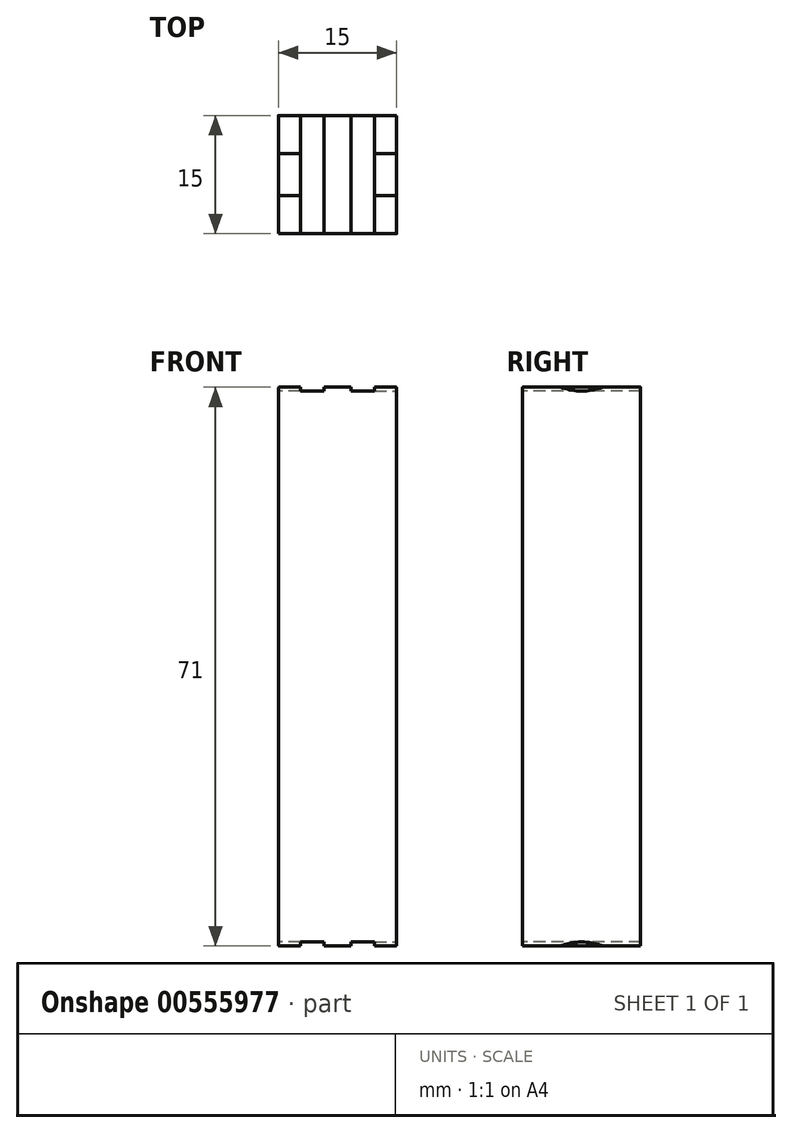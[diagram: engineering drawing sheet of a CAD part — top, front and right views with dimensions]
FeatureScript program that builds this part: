
annotation { "Feature Type Name" : "Feature", "Feature Type Description" : "" }
export const myFeature = defineFeature(function(context is Context, id is Id, definition is map)
    precondition{}
    {
        {
            assignVariable(context, id + "F0", {"name" : "length", "anyValue" : 30});
        }
        {
            var Q0;
            Q0=qCreatedBy(makeId("Right.planeOp"),FACE);
            var sketch = newSketch(context, id + "F1", { "sketchPlane" : qUnion([Q0])});
            skArc(sketch, "E0", {"start": v(7.5, 0) * mm, "mid": v(0, 7.5) * mm, "end": v(-7.5, 0) * mm});
            skCircle(sketch, "E1", {"center": v(0, 0) * mm, "radius": 2.5 * mm});
            skLineSegment(sketch, "E2", {"start": v(-7.5, 0) * mm, "end": v(-7.5, -12.5) * mm});
            skLineSegment(sketch, "E3", {"start": v(7.5, 0) * mm, "end": v(7.5, -12.5) * mm});
            skLineSegment(sketch, "E4", {"start": v(7.5, -12.5) * mm, "end": v(-7.5, -12.5) * mm});
            skSolve(sketch);
        }
        {
            var Q0;
            Q0=makeQuery(id+"F1.imprint","IMPRINT",FACE,{"disambiguationData":[TD([[makeQuery(id+"F1.imprint","IMPRINT",EDGE,{"derivedFrom":sQuery(id+"F1.wireOp",EDGE,"E0")}),1.0]])]});
            extrude(context, id + "F2", {"entities" : qUnion([Q0]), "depth" : 15 * mm, "symmetric" : true});
        }
        {
            var Q0;
            Q0=qCreatedBy(makeId("Front.planeOp"),FACE);
            var sketch = newSketch(context, id + "F3", { "sketchPlane" : qUnion([Q0])});
            skLineSegment(sketch, "E5", {"start": v(0, -18.95) * mm, "end": v(0, 19.26) * mm, "construction": true});
            skLineSegment(sketch, "E6", {"start": v(-12.45, 0) * mm, "end": v(16.05, 0) * mm, "construction": true});
            skLineSegment(sketch, "E7.0", {"start": v(-1.7, -7) * mm, "end": v(-1.7, 8.45) * mm});
            skLineSegment(sketch, "E8.0.MirrorCS", {"start": v(1.7, -7) * mm, "end": v(1.7, 8.45) * mm});
            skLineSegment(sketch, "E9.0", {"start": v(-8.58, -7) * mm, "end": v(-4.7, -7) * mm});
            skLineSegment(sketch, "E10.0", {"start": v(4.7, -7) * mm, "end": v(4.7, 8.45) * mm});
            skLineSegment(sketch, "E11.0", {"start": v(-4.7, -7) * mm, "end": v(-4.7, 8.45) * mm});
            skPoint(sketch, "E12.orphan", {"position": v(-1.7, -18.95) * mm});
            skLineSegment(sketch, "E13.trimOffspring", {"start": v(4.7, -7) * mm, "end": v(8.53, -7) * mm});
            skPoint(sketch, "E14.orphan", {"position": v(1.7, -18.95) * mm});
            skLineSegment(sketch, "E15", {"start": v(-8.58, 8.45) * mm, "end": v(-4.7, 8.45) * mm});
            skLineSegment(sketch, "E16", {"start": v(8.53, 8.45) * mm, "end": v(8.53, -7) * mm});
            skLineSegment(sketch, "E17", {"start": v(-8.58, -7) * mm, "end": v(-8.58, 8.45) * mm});
            skLineSegment(sketch, "E18.trimOffspring", {"start": v(-1.7, 8.45) * mm, "end": v(1.7, 8.45) * mm});
            skPoint(sketch, "E19.orphan", {"position": v(-1.7, 19.26) * mm});
            skPoint(sketch, "E20.orphan", {"position": v(1.7, 19.26) * mm});
            skLineSegment(sketch, "E21.trimOffspring", {"start": v(4.7, 8.45) * mm, "end": v(8.53, 8.45) * mm});
            skLineSegment(sketch, "E22", {"start": v(1.7, -7) * mm, "end": v(-1.7, -7) * mm});
            skSolve(sketch);
        }
        {
            var Q0;
            {Q0=qUnion([makeQuery(id+"F3.imprint","IMPRINT",FACE,{"disambiguationData":[TD([[makeQuery(id+"F3.imprint","IMPRINT",EDGE,{"derivedFrom":sQuery(id+"F3.wireOp",EDGE,"E7.0")}),-1.0]])]}),makeQuery(id+"F3.imprint","IMPRINT",FACE,{"disambiguationData":[TD([[makeQuery(id+"F3.imprint","IMPRINT",EDGE,{"derivedFrom":sQuery(id+"F3.wireOp",EDGE,"E9.0")}),1.0]])]}),makeQuery(id+"F3.imprint","IMPRINT",FACE,{"disambiguationData":[TD([[makeQuery(id+"F3.imprint","IMPRINT",EDGE,{"derivedFrom":sQuery(id+"F3.wireOp",EDGE,"E10.0")}),-1.0]])]})]);}
            extrude(context, id + "F4", {"entities" : qUnion([Q0]), "operationType" : NewBodyOperationType.REMOVE, "oppositeDirection" : true, "depth" : 32.83 * mm, "symmetric" : true});
        }
        {
            var Q0;
            Q0=makeQuery(id+"F2.opExtrude","CAP_FACE",FACE,{"disambiguationData":[OSD([sQuery(id+"F1.wireOp",EDGE,"E0"),sQuery(id+"F1.wireOp",EDGE,"E1"),sQuery(id+"F1.wireOp",EDGE,"E2"),sQuery(id+"F1.wireOp",EDGE,"E3"),sQuery(id+"F1.wireOp",EDGE,"E4")])],"isStart":true});
            var sketch = newSketch(context, id + "F5", { "sketchPlane" : qUnion([Q0])});
            skCircle(sketch, "E23", {"center": v(0, 0) * mm, "radius": 7.5 * mm});
            skSolve(sketch);
        }
        {
            var Q0;
            {var subQ0=makeQuery(id+"F4.boolean.opBoolean","INTERSECT",EDGE,{"derivedFrom":[makeQuery(id+"F2.opExtrude","CAP_FACE",FACE,{"disambiguationData":[OSD([sQuery(id+"F1.wireOp",EDGE,"E0"),sQuery(id+"F1.wireOp",EDGE,"E1"),sQuery(id+"F1.wireOp",EDGE,"E2"),sQuery(id+"F1.wireOp",EDGE,"E3"),sQuery(id+"F1.wireOp",EDGE,"E4")])],"isStart":true}),makeQuery(id+"F4.opExtrude","SWEPT_FACE",FACE,{"disambiguationData":[OSD([sQuery(id+"F3.wireOp",EDGE,"E9.0")])]})]});var subQ1=sQuery(id+"F5.wireOp",EDGE,"E23");var subQ3=makeQuery(id+"F5.imprint","INTERSECT",VERTEX,{"disambiguationData":[OD(0.0)],"derivedFrom":[subQ0,subQ1]});Q0=qUnion([makeQuery(id+"F5.imprint","IMPRINT",FACE,{"disambiguationData":[TD([[makeQuery(id+"F5.imprint","IMPRINT",EDGE,{"disambiguationData":[TD([[subQ3,-1.0]])],"derivedFrom":subQ1}),1.0]])]}),makeQuery(id+"F5.imprint","IMPRINT",FACE,{"disambiguationData":[TD([[makeQuery(id+"F5.imprint","IMPRINT",EDGE,{"disambiguationData":[TD([[subQ3,1.0]])],"derivedFrom":subQ1}),1.0]])]})]);}
            var Q1;
            Q1=makeQuery(id+"F4.boolean.opBoolean","COPY",FACE,{"derivedFrom":makeQuery(id+"F4.opExtrude","SWEPT_FACE",FACE,{"disambiguationData":[OSD([sQuery(id+"F3.wireOp",EDGE,"E11.0")])]})});
            extrude(context, id + "F6", {"entities" : qUnion([Q0]), "operationType" : NewBodyOperationType.REMOVE, "endBound" : BoundingType.UP_TO_SURFACE, "oppositeDirection" : true, "endBoundEntityFace" : qUnion([Q1]), "depth" : 25 * mm});
        }
        {
            var Q0;
            Q0=makeQuery(id+"F2.opExtrude","CAP_FACE",FACE,{"disambiguationData":[OSD([sQuery(id+"F1.wireOp",EDGE,"E0"),sQuery(id+"F1.wireOp",EDGE,"E1"),sQuery(id+"F1.wireOp",EDGE,"E2"),sQuery(id+"F1.wireOp",EDGE,"E3"),sQuery(id+"F1.wireOp",EDGE,"E4")])],"isStart":false});
            var sketch = newSketch(context, id + "F7", { "sketchPlane" : qUnion([Q0])});
            skCircle(sketch, "E24", {"center": v(0, 0) * mm, "radius": 7.5 * mm});
            skSolve(sketch);
        }
        {
            var Q0;
            {var subQ0=makeQuery(id+"F4.boolean.opBoolean","INTERSECT",EDGE,{"derivedFrom":[makeQuery(id+"F2.opExtrude","CAP_FACE",FACE,{"disambiguationData":[OSD([sQuery(id+"F1.wireOp",EDGE,"E0"),sQuery(id+"F1.wireOp",EDGE,"E1"),sQuery(id+"F1.wireOp",EDGE,"E2"),sQuery(id+"F1.wireOp",EDGE,"E3"),sQuery(id+"F1.wireOp",EDGE,"E4")])],"isStart":false}),makeQuery(id+"F4.opExtrude","SWEPT_FACE",FACE,{"disambiguationData":[OSD([sQuery(id+"F3.wireOp",EDGE,"E13.trimOffspring")])]})]});var subQ1=sQuery(id+"F7.wireOp",EDGE,"E24");var subQ3=makeQuery(id+"F7.imprint","INTERSECT",VERTEX,{"disambiguationData":[OD(0.0)],"derivedFrom":[subQ0,subQ1]});Q0=qUnion([makeQuery(id+"F7.imprint","IMPRINT",FACE,{"disambiguationData":[TD([[makeQuery(id+"F7.imprint","IMPRINT",EDGE,{"disambiguationData":[TD([[subQ3,1.0]])],"derivedFrom":subQ1}),1.0]])]}),makeQuery(id+"F7.imprint","IMPRINT",FACE,{"disambiguationData":[TD([[makeQuery(id+"F7.imprint","IMPRINT",EDGE,{"disambiguationData":[TD([[subQ3,-1.0]])],"derivedFrom":subQ1}),1.0]])]})]);}
            var Q1;
            Q1=makeQuery(id+"F4.boolean.opBoolean","COPY",FACE,{"derivedFrom":makeQuery(id+"F4.opExtrude","SWEPT_FACE",FACE,{"disambiguationData":[OSD([sQuery(id+"F3.wireOp",EDGE,"E10.0")])]})});
            extrude(context, id + "F8", {"entities" : qUnion([Q0]), "operationType" : NewBodyOperationType.REMOVE, "endBound" : BoundingType.UP_TO_SURFACE, "oppositeDirection" : true, "endBoundEntityFace" : qUnion([Q1]), "depth" : 25 * mm});
        }
        {
            var Q0;
            {var subQ0=sQuery(id+"F1.wireOp",EDGE,"E2");var subQ1=makeQuery(id+"F2.opExtrude","CAP_FACE",FACE,{"disambiguationData":[OSD([sQuery(id+"F1.wireOp",EDGE,"E0"),sQuery(id+"F1.wireOp",EDGE,"E1"),subQ0,sQuery(id+"F1.wireOp",EDGE,"E3"),sQuery(id+"F1.wireOp",EDGE,"E4")])],"isStart":false});var subQ2=makeQuery(id+"F4.opExtrude","SWEPT_FACE",FACE,{"disambiguationData":[OSD([sQuery(id+"F3.wireOp",EDGE,"E13.trimOffspring")])]});Q0=makeQuery(id+"F8.boolean.opBoolean","SPLIT",EDGE,{"disambiguationData":[TD([makeQuery(id+"F2.opExtrude","SWEPT_FACE",FACE,{"disambiguationData":[OSD([subQ0])]})])],"derivedFrom":makeQuery(id+"F4.boolean.opBoolean","INTERSECT",EDGE,{"derivedFrom":[subQ1,subQ2]})});}
            var Q1;
            Q1=makeQuery(id+"F8.boolean.opBoolean","COPY",EDGE,{"derivedFrom":makeQuery(id+"F8.opExtrude","CAP_EDGE",EDGE,{"disambiguationData":[OSD([sQuery(id+"F7.wireOp",EDGE,"E24")])],"isStart":true})});
            var Q2;
            {var subQ0=sQuery(id+"F1.wireOp",EDGE,"E3");var subQ1=makeQuery(id+"F2.opExtrude","CAP_FACE",FACE,{"disambiguationData":[OSD([sQuery(id+"F1.wireOp",EDGE,"E0"),sQuery(id+"F1.wireOp",EDGE,"E1"),sQuery(id+"F1.wireOp",EDGE,"E2"),subQ0,sQuery(id+"F1.wireOp",EDGE,"E4")])],"isStart":false});var subQ2=makeQuery(id+"F4.opExtrude","SWEPT_FACE",FACE,{"disambiguationData":[OSD([sQuery(id+"F3.wireOp",EDGE,"E13.trimOffspring")])]});Q2=makeQuery(id+"F8.boolean.opBoolean","SPLIT",EDGE,{"disambiguationData":[TD([makeQuery(id+"F2.opExtrude","SWEPT_FACE",FACE,{"disambiguationData":[OSD([subQ0])]})])],"derivedFrom":makeQuery(id+"F4.boolean.opBoolean","INTERSECT",EDGE,{"derivedFrom":[subQ1,subQ2]})});}
            var Q3;
            {var subQ0=sQuery(id+"F1.wireOp",EDGE,"E3");var subQ1=makeQuery(id+"F2.opExtrude","CAP_FACE",FACE,{"disambiguationData":[OSD([sQuery(id+"F1.wireOp",EDGE,"E0"),sQuery(id+"F1.wireOp",EDGE,"E1"),sQuery(id+"F1.wireOp",EDGE,"E2"),subQ0,sQuery(id+"F1.wireOp",EDGE,"E4")])],"isStart":true});var subQ2=makeQuery(id+"F4.opExtrude","SWEPT_FACE",FACE,{"disambiguationData":[OSD([sQuery(id+"F3.wireOp",EDGE,"E9.0")])]});Q3=makeQuery(id+"F6.boolean.opBoolean","SPLIT",EDGE,{"disambiguationData":[TD([makeQuery(id+"F2.opExtrude","SWEPT_FACE",FACE,{"disambiguationData":[OSD([subQ0])]})])],"derivedFrom":makeQuery(id+"F4.boolean.opBoolean","INTERSECT",EDGE,{"derivedFrom":[subQ1,subQ2]})});}
            var Q4;
            Q4=makeQuery(id+"F6.boolean.opBoolean","COPY",EDGE,{"derivedFrom":makeQuery(id+"F6.opExtrude","CAP_EDGE",EDGE,{"disambiguationData":[OSD([sQuery(id+"F5.wireOp",EDGE,"E23")])],"isStart":true})});
            var Q5;
            {var subQ0=sQuery(id+"F1.wireOp",EDGE,"E2");var subQ1=makeQuery(id+"F2.opExtrude","CAP_FACE",FACE,{"disambiguationData":[OSD([sQuery(id+"F1.wireOp",EDGE,"E0"),sQuery(id+"F1.wireOp",EDGE,"E1"),subQ0,sQuery(id+"F1.wireOp",EDGE,"E3"),sQuery(id+"F1.wireOp",EDGE,"E4")])],"isStart":true});var subQ2=makeQuery(id+"F4.opExtrude","SWEPT_FACE",FACE,{"disambiguationData":[OSD([sQuery(id+"F3.wireOp",EDGE,"E9.0")])]});Q5=makeQuery(id+"F6.boolean.opBoolean","SPLIT",EDGE,{"disambiguationData":[TD([makeQuery(id+"F2.opExtrude","SWEPT_FACE",FACE,{"disambiguationData":[OSD([subQ0])]})])],"derivedFrom":makeQuery(id+"F4.boolean.opBoolean","INTERSECT",EDGE,{"derivedFrom":[subQ1,subQ2]})});}
            fillet(context, id + "F9", {"entities" : qUnion([Q0, Q1, Q2, Q3, Q4, Q5]), "radius" : .1 * mm, "tangentPropagation" : true, "allowEdgeOverflow" : false});
        }
        {
            var Q0;
            Q0=qCreatedBy(makeId("Right.planeOp"),FACE);
            var sketch = newSketch(context, id + "F10", { "sketchPlane" : qUnion([Q0])});
            skArc(sketch, "E25", {"start": v(-7.5, 0) * mm, "mid": v(0, -7.5) * mm, "end": v(7.5, 0) * mm});
            skCircle(sketch, "E26", {"center": v(0, 0) * mm, "radius": 2.5 * mm});
            skLineSegment(sketch, "E27", {"start": v(7.5, 0) * mm, "end": v(7.5, 15.09) * mm});
            skLineSegment(sketch, "E28", {"start": v(-7.5, 0) * mm, "end": v(-7.5, 15.09) * mm});
            skLineSegment(sketch, "E29", {"start": v(7.5, 15.09) * mm, "end": v(-7.5, 15.09) * mm});
            skSolve(sketch);
        }
        {
            var Q0;
            Q0=makeQuery(id+"F10.imprint","IMPRINT",FACE,{"disambiguationData":[TD([[makeQuery(id+"F10.imprint","IMPRINT",EDGE,{"derivedFrom":sQuery(id+"F10.wireOp",EDGE,"E25")}),1.0]])]});
            extrude(context, id + "F11", {"entities" : qUnion([Q0]), "depth" : 15 * mm, "symmetric" : true});
        }
        {
            var Q0;
            Q0=makeQuery(id+"F2.opExtrude","SWEPT_FACE",FACE,{"disambiguationData":[OSD([sQuery(id+"F1.wireOp",EDGE,"E2")])]});
            var sketch = newSketch(context, id + "F12", { "sketchPlane" : qUnion([Q0])});
            skLineSegment(sketch, "E30", {"start": v(-4.7, -7.5) * mm, "end": v(-4.7, 7.56) * mm});
            skLineSegment(sketch, "E31", {"start": v(-1.7, 7.56) * mm, "end": v(-1.7, -7.5) * mm});
            skLineSegment(sketch, "E32", {"start": v(1.7, -7.5) * mm, "end": v(1.7, 7.56) * mm});
            skLineSegment(sketch, "E33", {"start": v(4.7, 7.56) * mm, "end": v(4.7, -7.5) * mm});
            skLineSegment(sketch, "E34", {"start": v(-8.82, 0) * mm, "end": v(9.54, 0) * mm, "construction": true});
            skLineSegment(sketch, "E35.0", {"start": v(-4.7, 7.56) * mm, "end": v(-1.7, 7.56) * mm});
            skLineSegment(sketch, "E36.trimOffspring", {"start": v(1.7, 7.56) * mm, "end": v(4.7, 7.56) * mm});
            skLineSegment(sketch, "E37", {"start": v(-4.7, -7.5) * mm, "end": v(-1.7, -7.5) * mm});
            skLineSegment(sketch, "E38", {"start": v(1.7, -7.5) * mm, "end": v(4.7, -7.5) * mm});
            skSolve(sketch);
        }
        {
            var Q0;
            {var subQ7=sQuery(id+"F12.wireOp",EDGE,"E35.0");var subQ8=sQuery(id+"F12.wireOp",EDGE,"E31");var subQ14=sQuery(id+"F12.wireOp",EDGE,"E36.trimOffspring");var subQ19=sQuery(id+"F12.wireOp",EDGE,"E37");var subQ21=makeQuery(id+"F12.imprint","INTERSECT",VERTEX,{"derivedFrom":[subQ8,subQ19]});var subQ25=sQuery(id+"F12.wireOp",EDGE,"E38");Q0=qUnion([makeQuery(id+"F12.imprint","IMPRINT",FACE,{"disambiguationData":[TD([[makeQuery(id+"F12.imprint","IMPRINT",EDGE,{"derivedFrom":subQ7}),-1.0]])]}),makeQuery(id+"F12.imprint","IMPRINT",FACE,{"disambiguationData":[TD([[makeQuery(id+"F12.imprint","IMPRINT",EDGE,{"derivedFrom":subQ14}),-1.0]])]}),makeQuery(id+"F12.imprint","IMPRINT",FACE,{"disambiguationData":[TD([[makeQuery(id+"F12.imprint","IMPRINT",EDGE,{"disambiguationData":[TD([[subQ21,1.0]])],"derivedFrom":subQ19}),1.0]])]}),makeQuery(id+"F12.imprint","IMPRINT",FACE,{"disambiguationData":[TD([[makeQuery(id+"F12.imprint","IMPRINT",EDGE,{"derivedFrom":subQ25}),1.0]])]})]);}
            extrude(context, id + "F13", {"entities" : qUnion([Q0]), "operationType" : NewBodyOperationType.REMOVE, "endBound" : BoundingType.THROUGH_ALL, "oppositeDirection" : true, "depth" : 25 * mm});
        }
        {
            var Q0;
            Q0=makeQuery(id+"F11.opExtrude","CAP_EDGE",EDGE,{"disambiguationData":[OSD([sQuery(id+"F10.wireOp",EDGE,"E27")])],"isStart":true});
            var Q1;
            Q1=makeQuery(id+"FippyAewqrXsgNA_2.boolean.opBoolean","INTERSECT",EDGE,{"derivedFrom":[makeQuery(id+"F11.opExtrude","CAP_FACE",FACE,{"disambiguationData":[OSD([sQuery(id+"F10.wireOp",EDGE,"E25"),sQuery(id+"F10.wireOp",EDGE,"E26"),sQuery(id+"F10.wireOp",EDGE,"E27"),sQuery(id+"F10.wireOp",EDGE,"E28"),sQuery(id+"F10.wireOp",EDGE,"E29")])],"isStart":true}),makeQuery(id+"FippyAewqrXsgNA_2.opExtrude","SWEPT_FACE",FACE,{"disambiguationData":[OSD([sQuery(id+"F3mLFsG5Fno42gm_2.wireOp",EDGE,"c0f086f1-8268-42b0-bca9-d790b92bd122")])]})]});
            var Q2;
            Q2=makeQuery(id+"FippyAewqrXsgNA_2.boolean.opBoolean","INTERSECT",EDGE,{"derivedFrom":[makeQuery(id+"F11.opExtrude","CAP_FACE",FACE,{"disambiguationData":[OSD([sQuery(id+"F10.wireOp",EDGE,"E25"),sQuery(id+"F10.wireOp",EDGE,"E26"),sQuery(id+"F10.wireOp",EDGE,"E27"),sQuery(id+"F10.wireOp",EDGE,"E28"),sQuery(id+"F10.wireOp",EDGE,"E29")])],"isStart":true}),makeQuery(id+"FippyAewqrXsgNA_2.opExtrude","SWEPT_FACE",FACE,{"disambiguationData":[OSD([sQuery(id+"F3mLFsG5Fno42gm_2.wireOp",EDGE,"249a57c8-6c74-4b6e-b988-dad3f8593ead.filletArc")])]})]});
            var Q3;
            Q3=makeQuery(id+"FippyAewqrXsgNA_2.boolean.opBoolean","INTERSECT",EDGE,{"derivedFrom":[makeQuery(id+"F11.opExtrude","CAP_FACE",FACE,{"disambiguationData":[OSD([sQuery(id+"F10.wireOp",EDGE,"E25"),sQuery(id+"F10.wireOp",EDGE,"E26"),sQuery(id+"F10.wireOp",EDGE,"E27"),sQuery(id+"F10.wireOp",EDGE,"E28"),sQuery(id+"F10.wireOp",EDGE,"E29")])],"isStart":true}),makeQuery(id+"FippyAewqrXsgNA_2.opExtrude","SWEPT_FACE",FACE,{"disambiguationData":[OSD([sQuery(id+"F3mLFsG5Fno42gm_2.wireOp",EDGE,"efa5c192-3512-44de-8fa8-280cfb2f5b3e.0")])]})]});
            var Q4;
            Q4=makeQuery(id+"FippyAewqrXsgNA_2.boolean.opBoolean","INTERSECT",EDGE,{"derivedFrom":[makeQuery(id+"F11.opExtrude","CAP_FACE",FACE,{"disambiguationData":[OSD([sQuery(id+"F10.wireOp",EDGE,"E25"),sQuery(id+"F10.wireOp",EDGE,"E26"),sQuery(id+"F10.wireOp",EDGE,"E27"),sQuery(id+"F10.wireOp",EDGE,"E28"),sQuery(id+"F10.wireOp",EDGE,"E29")])],"isStart":true}),makeQuery(id+"FippyAewqrXsgNA_2.opExtrude","SWEPT_FACE",FACE,{"disambiguationData":[OSD([sQuery(id+"F3mLFsG5Fno42gm_2.wireOp",EDGE,"8754f7bb-135e-456f-a92c-7c412a1b982e.filletArc")])]})]});
            var Q5;
            Q5=makeQuery(id+"FippyAewqrXsgNA_2.boolean.opBoolean","INTERSECT",EDGE,{"derivedFrom":[makeQuery(id+"F11.opExtrude","CAP_FACE",FACE,{"disambiguationData":[OSD([sQuery(id+"F10.wireOp",EDGE,"E25"),sQuery(id+"F10.wireOp",EDGE,"E26"),sQuery(id+"F10.wireOp",EDGE,"E27"),sQuery(id+"F10.wireOp",EDGE,"E28"),sQuery(id+"F10.wireOp",EDGE,"E29")])],"isStart":true}),makeQuery(id+"FippyAewqrXsgNA_2.opExtrude","SWEPT_FACE",FACE,{"disambiguationData":[OSD([sQuery(id+"F3mLFsG5Fno42gm_2.wireOp",EDGE,"867f090d-7a0f-47e4-ad42-8750be9dd33b")])]}),makeQuery(id+"FippyAewqrXsgNA_2.opExtrude","SWEPT_FACE",FACE,{"disambiguationData":[OSD([sQuery(id+"F3mLFsG5Fno42gm_2.wireOp",EDGE,"97be5439-c5b2-4738-be54-ead6327fe10f.trimOffspring")])]})]});
            var Q6;
            Q6=makeQuery(id+"FippyAewqrXsgNA_2.boolean.opBoolean","INTERSECT",EDGE,{"derivedFrom":[makeQuery(id+"F11.opExtrude","CAP_FACE",FACE,{"disambiguationData":[OSD([sQuery(id+"F10.wireOp",EDGE,"E25"),sQuery(id+"F10.wireOp",EDGE,"E26"),sQuery(id+"F10.wireOp",EDGE,"E27"),sQuery(id+"F10.wireOp",EDGE,"E28"),sQuery(id+"F10.wireOp",EDGE,"E29")])],"isStart":true}),makeQuery(id+"FippyAewqrXsgNA_2.opExtrude","SWEPT_FACE",FACE,{"disambiguationData":[OSD([sQuery(id+"F3mLFsG5Fno42gm_2.wireOp",EDGE,"c7209cef-6667-47b6-a156-e2bdf9a25917.filletArc")])]})]});
            var Q7;
            Q7=makeQuery(id+"FippyAewqrXsgNA_2.boolean.opBoolean","INTERSECT",EDGE,{"derivedFrom":[makeQuery(id+"F11.opExtrude","CAP_FACE",FACE,{"disambiguationData":[OSD([sQuery(id+"F10.wireOp",EDGE,"E25"),sQuery(id+"F10.wireOp",EDGE,"E26"),sQuery(id+"F10.wireOp",EDGE,"E27"),sQuery(id+"F10.wireOp",EDGE,"E28"),sQuery(id+"F10.wireOp",EDGE,"E29")])],"isStart":true}),makeQuery(id+"FippyAewqrXsgNA_2.opExtrude","SWEPT_FACE",FACE,{"disambiguationData":[OSD([sQuery(id+"F3mLFsG5Fno42gm_2.wireOp",EDGE,"dcbcf22c-f553-4f41-875d-d37e6c168270.0")])]})]});
            var Q8;
            Q8=makeQuery(id+"FippyAewqrXsgNA_2.boolean.opBoolean","INTERSECT",EDGE,{"derivedFrom":[makeQuery(id+"F11.opExtrude","CAP_FACE",FACE,{"disambiguationData":[OSD([sQuery(id+"F10.wireOp",EDGE,"E25"),sQuery(id+"F10.wireOp",EDGE,"E26"),sQuery(id+"F10.wireOp",EDGE,"E27"),sQuery(id+"F10.wireOp",EDGE,"E28"),sQuery(id+"F10.wireOp",EDGE,"E29")])],"isStart":true}),makeQuery(id+"FippyAewqrXsgNA_2.opExtrude","SWEPT_FACE",FACE,{"disambiguationData":[OSD([sQuery(id+"F3mLFsG5Fno42gm_2.wireOp",EDGE,"fd427596-af6b-4541-8bac-1afcfd813c00.filletArc")])]})]});
            var Q9;
            Q9=makeQuery(id+"FippyAewqrXsgNA_2.boolean.opBoolean","INTERSECT",EDGE,{"derivedFrom":[makeQuery(id+"F11.opExtrude","CAP_FACE",FACE,{"disambiguationData":[OSD([sQuery(id+"F10.wireOp",EDGE,"E25"),sQuery(id+"F10.wireOp",EDGE,"E26"),sQuery(id+"F10.wireOp",EDGE,"E27"),sQuery(id+"F10.wireOp",EDGE,"E28"),sQuery(id+"F10.wireOp",EDGE,"E29")])],"isStart":true}),makeQuery(id+"FippyAewqrXsgNA_2.opExtrude","SWEPT_FACE",FACE,{"disambiguationData":[OSD([sQuery(id+"F3mLFsG5Fno42gm_2.wireOp",EDGE,"bfd3914a-7e03-41c0-b127-95db132ec3d2.trimOffspring")])]})]});
            var Q10;
            Q10=makeQuery(id+"F11.opExtrude","CAP_EDGE",EDGE,{"disambiguationData":[OSD([sQuery(id+"F10.wireOp",EDGE,"E28")])],"isStart":true});
            var Q11;
            Q11=makeQuery(id+"F11.opExtrude","CAP_EDGE",EDGE,{"disambiguationData":[OSD([sQuery(id+"F10.wireOp",EDGE,"E27")])],"isStart":false});
            var Q12;
            Q12=makeQuery(id+"FippyAewqrXsgNA_2.boolean.opBoolean","INTERSECT",EDGE,{"derivedFrom":[makeQuery(id+"F11.opExtrude","CAP_FACE",FACE,{"disambiguationData":[OSD([sQuery(id+"F10.wireOp",EDGE,"E25"),sQuery(id+"F10.wireOp",EDGE,"E26"),sQuery(id+"F10.wireOp",EDGE,"E27"),sQuery(id+"F10.wireOp",EDGE,"E28"),sQuery(id+"F10.wireOp",EDGE,"E29")])],"isStart":false}),makeQuery(id+"FippyAewqrXsgNA_2.opExtrude","SWEPT_FACE",FACE,{"disambiguationData":[OSD([sQuery(id+"F3mLFsG5Fno42gm_2.wireOp",EDGE,"c0f086f1-8268-42b0-bca9-d790b92bd122")])]})]});
            var Q13;
            Q13=makeQuery(id+"FippyAewqrXsgNA_2.boolean.opBoolean","INTERSECT",EDGE,{"derivedFrom":[makeQuery(id+"F11.opExtrude","CAP_FACE",FACE,{"disambiguationData":[OSD([sQuery(id+"F10.wireOp",EDGE,"E25"),sQuery(id+"F10.wireOp",EDGE,"E26"),sQuery(id+"F10.wireOp",EDGE,"E27"),sQuery(id+"F10.wireOp",EDGE,"E28"),sQuery(id+"F10.wireOp",EDGE,"E29")])],"isStart":false}),makeQuery(id+"FippyAewqrXsgNA_2.opExtrude","SWEPT_FACE",FACE,{"disambiguationData":[OSD([sQuery(id+"F3mLFsG5Fno42gm_2.wireOp",EDGE,"249a57c8-6c74-4b6e-b988-dad3f8593ead.filletArc")])]})]});
            var Q14;
            Q14=makeQuery(id+"FippyAewqrXsgNA_2.boolean.opBoolean","INTERSECT",EDGE,{"derivedFrom":[makeQuery(id+"F11.opExtrude","CAP_FACE",FACE,{"disambiguationData":[OSD([sQuery(id+"F10.wireOp",EDGE,"E25"),sQuery(id+"F10.wireOp",EDGE,"E26"),sQuery(id+"F10.wireOp",EDGE,"E27"),sQuery(id+"F10.wireOp",EDGE,"E28"),sQuery(id+"F10.wireOp",EDGE,"E29")])],"isStart":false}),makeQuery(id+"FippyAewqrXsgNA_2.opExtrude","SWEPT_FACE",FACE,{"disambiguationData":[OSD([sQuery(id+"F3mLFsG5Fno42gm_2.wireOp",EDGE,"efa5c192-3512-44de-8fa8-280cfb2f5b3e.0")])]})]});
            var Q15;
            Q15=makeQuery(id+"FippyAewqrXsgNA_2.boolean.opBoolean","INTERSECT",EDGE,{"derivedFrom":[makeQuery(id+"F11.opExtrude","CAP_FACE",FACE,{"disambiguationData":[OSD([sQuery(id+"F10.wireOp",EDGE,"E25"),sQuery(id+"F10.wireOp",EDGE,"E26"),sQuery(id+"F10.wireOp",EDGE,"E27"),sQuery(id+"F10.wireOp",EDGE,"E28"),sQuery(id+"F10.wireOp",EDGE,"E29")])],"isStart":false}),makeQuery(id+"FippyAewqrXsgNA_2.opExtrude","SWEPT_FACE",FACE,{"disambiguationData":[OSD([sQuery(id+"F3mLFsG5Fno42gm_2.wireOp",EDGE,"8754f7bb-135e-456f-a92c-7c412a1b982e.filletArc")])]})]});
            var Q16;
            Q16=makeQuery(id+"FippyAewqrXsgNA_2.boolean.opBoolean","INTERSECT",EDGE,{"derivedFrom":[makeQuery(id+"F11.opExtrude","CAP_FACE",FACE,{"disambiguationData":[OSD([sQuery(id+"F10.wireOp",EDGE,"E25"),sQuery(id+"F10.wireOp",EDGE,"E26"),sQuery(id+"F10.wireOp",EDGE,"E27"),sQuery(id+"F10.wireOp",EDGE,"E28"),sQuery(id+"F10.wireOp",EDGE,"E29")])],"isStart":false}),makeQuery(id+"FippyAewqrXsgNA_2.opExtrude","SWEPT_FACE",FACE,{"disambiguationData":[OSD([sQuery(id+"F3mLFsG5Fno42gm_2.wireOp",EDGE,"867f090d-7a0f-47e4-ad42-8750be9dd33b")])]}),makeQuery(id+"FippyAewqrXsgNA_2.opExtrude","SWEPT_FACE",FACE,{"disambiguationData":[OSD([sQuery(id+"F3mLFsG5Fno42gm_2.wireOp",EDGE,"97be5439-c5b2-4738-be54-ead6327fe10f.trimOffspring")])]})]});
            var Q17;
            Q17=makeQuery(id+"FippyAewqrXsgNA_2.boolean.opBoolean","INTERSECT",EDGE,{"derivedFrom":[makeQuery(id+"F11.opExtrude","CAP_FACE",FACE,{"disambiguationData":[OSD([sQuery(id+"F10.wireOp",EDGE,"E25"),sQuery(id+"F10.wireOp",EDGE,"E26"),sQuery(id+"F10.wireOp",EDGE,"E27"),sQuery(id+"F10.wireOp",EDGE,"E28"),sQuery(id+"F10.wireOp",EDGE,"E29")])],"isStart":false}),makeQuery(id+"FippyAewqrXsgNA_2.opExtrude","SWEPT_FACE",FACE,{"disambiguationData":[OSD([sQuery(id+"F3mLFsG5Fno42gm_2.wireOp",EDGE,"c7209cef-6667-47b6-a156-e2bdf9a25917.filletArc")])]})]});
            var Q18;
            Q18=makeQuery(id+"FippyAewqrXsgNA_2.boolean.opBoolean","INTERSECT",EDGE,{"derivedFrom":[makeQuery(id+"F11.opExtrude","CAP_FACE",FACE,{"disambiguationData":[OSD([sQuery(id+"F10.wireOp",EDGE,"E25"),sQuery(id+"F10.wireOp",EDGE,"E26"),sQuery(id+"F10.wireOp",EDGE,"E27"),sQuery(id+"F10.wireOp",EDGE,"E28"),sQuery(id+"F10.wireOp",EDGE,"E29")])],"isStart":false}),makeQuery(id+"FippyAewqrXsgNA_2.opExtrude","SWEPT_FACE",FACE,{"disambiguationData":[OSD([sQuery(id+"F3mLFsG5Fno42gm_2.wireOp",EDGE,"dcbcf22c-f553-4f41-875d-d37e6c168270.0")])]})]});
            var Q19;
            Q19=makeQuery(id+"FippyAewqrXsgNA_2.boolean.opBoolean","INTERSECT",EDGE,{"derivedFrom":[makeQuery(id+"F11.opExtrude","CAP_FACE",FACE,{"disambiguationData":[OSD([sQuery(id+"F10.wireOp",EDGE,"E25"),sQuery(id+"F10.wireOp",EDGE,"E26"),sQuery(id+"F10.wireOp",EDGE,"E27"),sQuery(id+"F10.wireOp",EDGE,"E28"),sQuery(id+"F10.wireOp",EDGE,"E29")])],"isStart":false}),makeQuery(id+"FippyAewqrXsgNA_2.opExtrude","SWEPT_FACE",FACE,{"disambiguationData":[OSD([sQuery(id+"F3mLFsG5Fno42gm_2.wireOp",EDGE,"fd427596-af6b-4541-8bac-1afcfd813c00.filletArc")])]})]});
            var Q20;
            Q20=makeQuery(id+"FippyAewqrXsgNA_2.boolean.opBoolean","INTERSECT",EDGE,{"derivedFrom":[makeQuery(id+"F11.opExtrude","CAP_FACE",FACE,{"disambiguationData":[OSD([sQuery(id+"F10.wireOp",EDGE,"E25"),sQuery(id+"F10.wireOp",EDGE,"E26"),sQuery(id+"F10.wireOp",EDGE,"E27"),sQuery(id+"F10.wireOp",EDGE,"E28"),sQuery(id+"F10.wireOp",EDGE,"E29")])],"isStart":false}),makeQuery(id+"FippyAewqrXsgNA_2.opExtrude","SWEPT_FACE",FACE,{"disambiguationData":[OSD([sQuery(id+"F3mLFsG5Fno42gm_2.wireOp",EDGE,"bfd3914a-7e03-41c0-b127-95db132ec3d2.trimOffspring")])]})]});
            var Q21;
            Q21=makeQuery(id+"F11.opExtrude","CAP_EDGE",EDGE,{"disambiguationData":[OSD([sQuery(id+"F10.wireOp",EDGE,"E28")])],"isStart":false});
            fillet(context, id + "F14", {"entities" : qUnion([Q0, Q1, Q2, Q3, Q4, Q5, Q6, Q7, Q8, Q9, Q10, Q11, Q12, Q13, Q14, Q15, Q16, Q17, Q18, Q19, Q20, Q21]), "radius" : .1 * mm, "tangentPropagation" : true, "allowEdgeOverflow" : false});
        }
        {
            var Q0;
            Q0=makeQuery(id+"F11.opExtrude","SWEPT_BODY",BODY,{"disambiguationData":[OSD([sQuery(id+"F10.wireOp",EDGE,"E25"),sQuery(id+"F10.wireOp",EDGE,"E26"),sQuery(id+"F10.wireOp",EDGE,"E27"),sQuery(id+"F10.wireOp",EDGE,"E28"),sQuery(id+"F10.wireOp",EDGE,"E29")])]});
            deleteBodies(context, id + "F15", {"entities" : qUnion([Q0])});
        }
        {
            var Q0;
            Q0=makeQuery(id+"F2.opExtrude","SWEPT_FACE",FACE,{"disambiguationData":[OSD([sQuery(id+"F1.wireOp",EDGE,"E4")])]});
            var sketch = newSketch(context, id + "F16", { "sketchPlane" : qUnion([Q0])});
            skLineSegment(sketch, "E39.bottom", {"start": v(7.5, 7.52) * mm, "end": v(-7.5, 7.52) * mm});
            skLineSegment(sketch, "E39.top", {"start": v(7.5, -7.52) * mm, "end": v(-7.5, -7.52) * mm});
            skLineSegment(sketch, "E39.left", {"start": v(7.5, 7.52) * mm, "end": v(7.5, -7.52) * mm});
            skLineSegment(sketch, "E39.right", {"start": v(-7.5, 7.52) * mm, "end": v(-7.5, -7.52) * mm});
            skPoint(sketch, "E39.middle", {"position": v(0, 0) * mm});
            skSolve(sketch);
        }
        {
            var Q0;
            {var subQ1=sQuery(id+"F1.wireOp",EDGE,"E4");var subQ2=makeQuery(id+"F2.opExtrude","SWEPT_EDGE",EDGE,{"disambiguationData":[OSD([sQuery(id+"F1.wireOp",EDGE,"E2"),subQ1])]});Q0=makeQuery(id+"F16.imprint","IMPRINT",FACE,{"disambiguationData":[TD([[makeQuery(id+"F16.imprint","IMPRINT",EDGE,{"derivedFrom":subQ2}),1.0]])]});}
            extrude(context, id + "F17", {"entities" : qUnion([Q0]), "operationType" : NewBodyOperationType.ADD, "depth" : (getVariable(context, 'length')) * mm, "offsetDistance" : 25 * mm});
        }
        {
            var Q0;
            Q0=makeQuery(id+"F2.opExtrude","SWEPT_BODY",BODY,{"disambiguationData":[OSD([sQuery(id+"F1.wireOp",EDGE,"E0"),sQuery(id+"F1.wireOp",EDGE,"E1"),sQuery(id+"F1.wireOp",EDGE,"E2"),sQuery(id+"F1.wireOp",EDGE,"E3"),sQuery(id+"F1.wireOp",EDGE,"E4")])]});
            var Q1;
            Q1=makeQuery(id+"F17.opExtrude","CAP_FACE",FACE,{"disambiguationData":[OSD([sQuery(id+"F1.wireOp",EDGE,"E2"),sQuery(id+"F1.wireOp",EDGE,"E3"),sQuery(id+"F1.wireOp",EDGE,"E4"),sQuery(id+"F16.wireOp",EDGE,"E39.left"),sQuery(id+"F16.wireOp",EDGE,"E39.right")])],"isStart":false});
            mirror(context, id + "F18", {"operationType" : NewBodyOperationType.ADD, "entities" : qUnion([Q0]), "mirrorPlane" : qUnion([Q1])});
        }
    });
